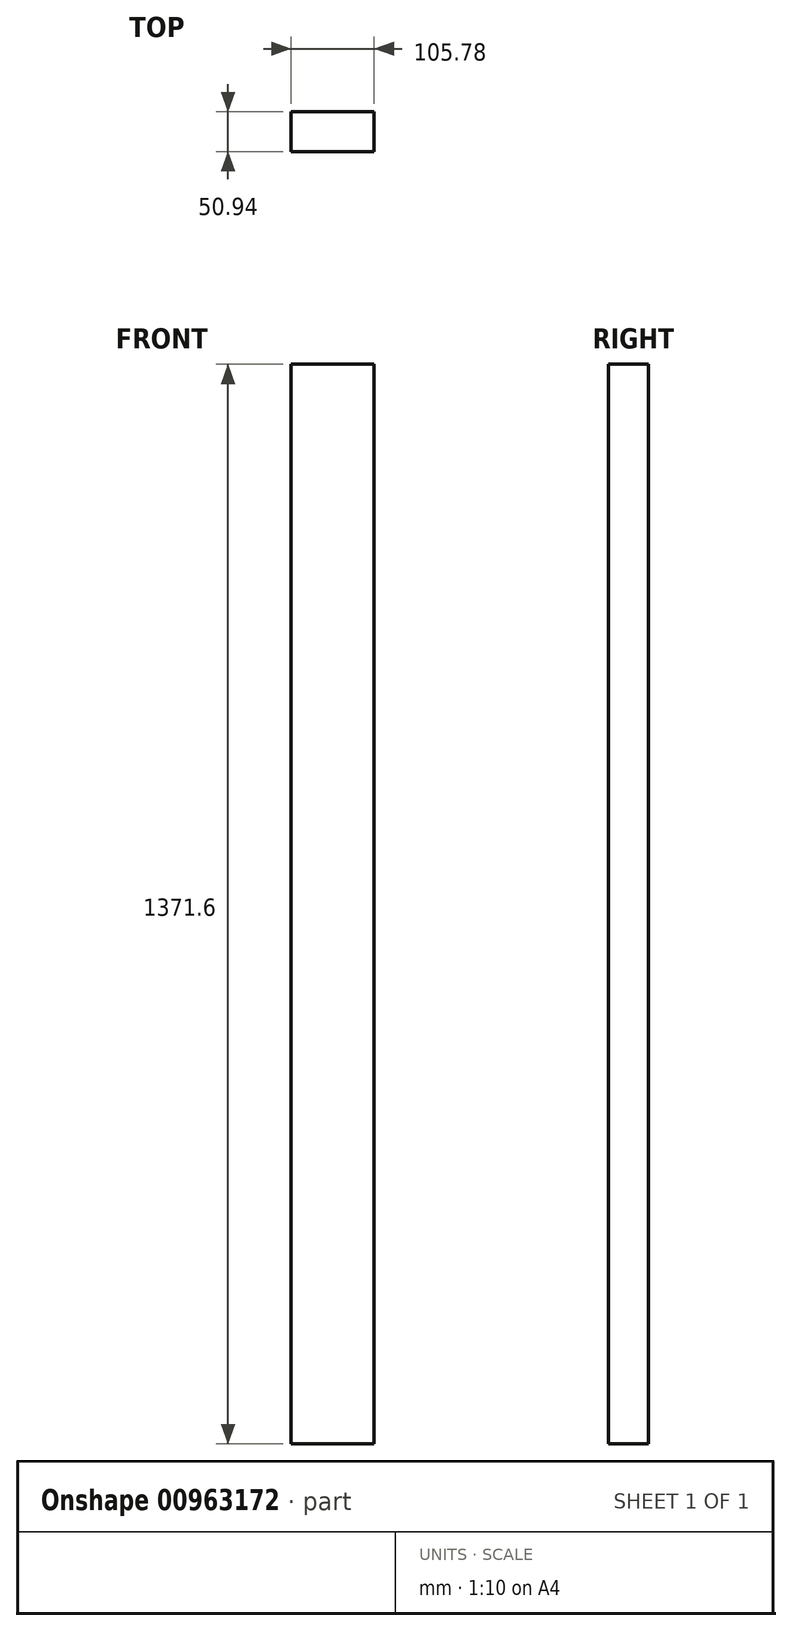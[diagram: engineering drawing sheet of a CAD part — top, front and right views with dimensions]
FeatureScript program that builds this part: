
annotation { "Feature Type Name" : "Feature", "Feature Type Description" : "" }
export const myFeature = defineFeature(function(context is Context, id is Id, definition is map)
    precondition{}
    {
        {
            var Q0;
            Q0=qCreatedBy(makeId("Top.planeOp"),FACE);
            var sketch = newSketch(context, id + "F0", { "sketchPlane" : qUnion([Q0])});
            skLineSegment(sketch, "E0.bottom", {"start": v(-52.89, -25.47) * mm, "end": v(52.89, -25.47) * mm});
            skLineSegment(sketch, "E0.top", {"start": v(-52.89, 25.47) * mm, "end": v(52.89, 25.47) * mm});
            skLineSegment(sketch, "E0.left", {"start": v(-52.89, -25.47) * mm, "end": v(-52.89, 25.47) * mm});
            skLineSegment(sketch, "E0.right", {"start": v(52.89, -25.47) * mm, "end": v(52.89, 25.47) * mm});
            skPoint(sketch, "E0.middle", {"position": v(0, 0) * mm});
            skSolve(sketch);
        }
        {
            var Q0;
            Q0=makeQuery(id+"F0.imprint","IMPRINT",FACE,{"disambiguationData":[TD([[makeQuery(id+"F0.imprint","IMPRINT",EDGE,{"derivedFrom":sQuery(id+"F0.wireOp",EDGE,"E0.bottom")}),1.0]])]});
            extrude(context, id + "F1", {"entities" : qUnion([Q0]), "depth" : 1371.6 * mm, "offsetDistance" : 25.4 * mm});
        }
    });
